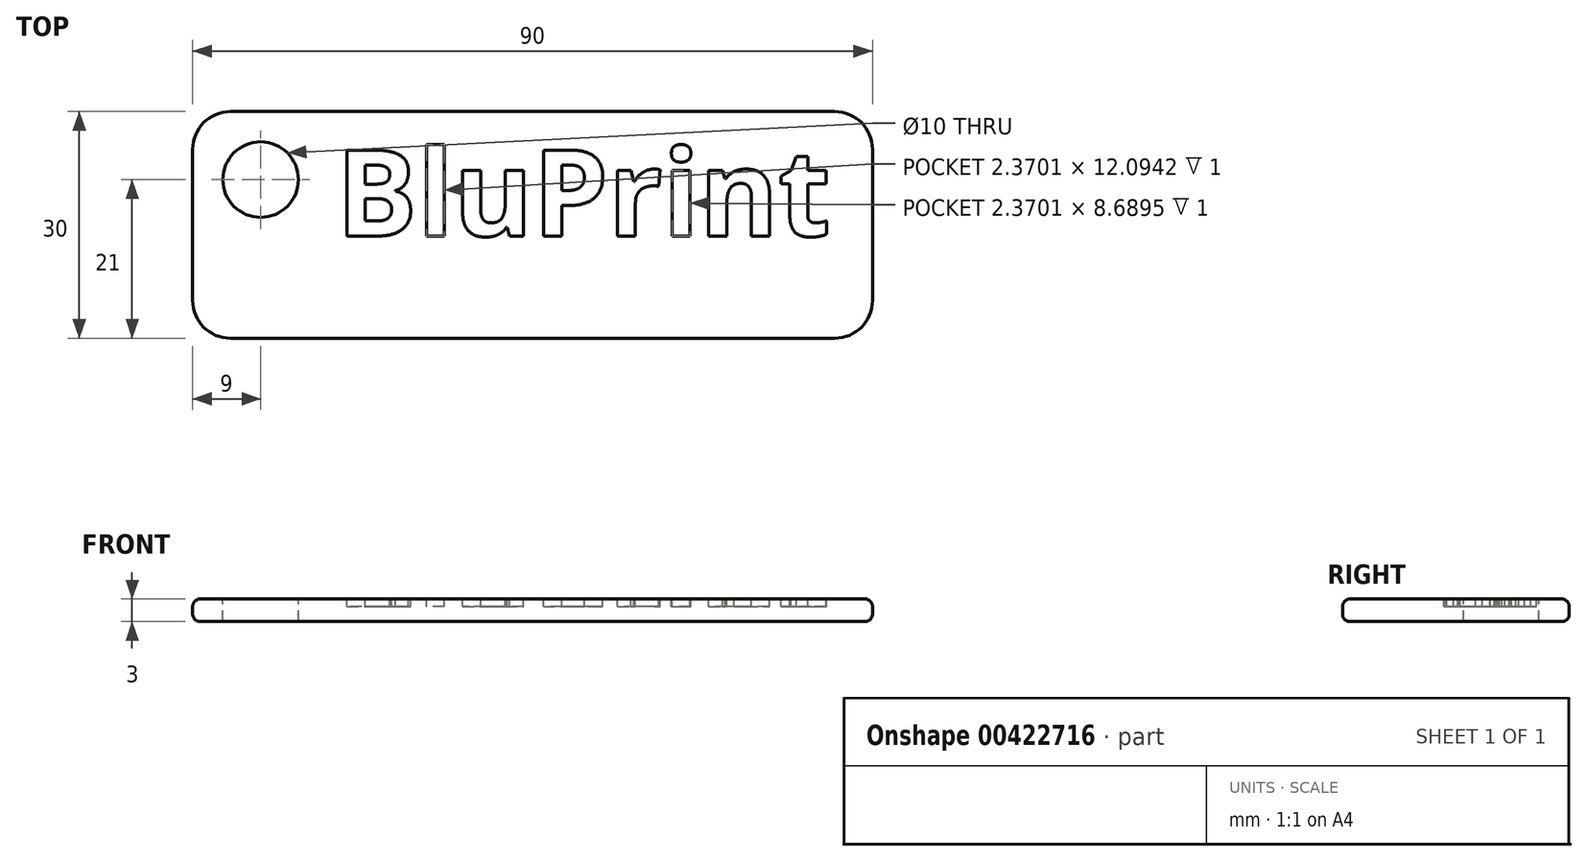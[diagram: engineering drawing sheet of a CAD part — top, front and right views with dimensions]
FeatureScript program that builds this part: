
annotation { "Feature Type Name" : "Feature", "Feature Type Description" : "" }
export const myFeature = defineFeature(function(context is Context, id is Id, definition is map)
    precondition{}
    {
        {
            var Q0;
            Q0=qCreatedBy(makeId("Top.planeOp"),FACE);
            var sketch = newSketch(context, id + "F0", { "sketchPlane" : qUnion([Q0])});
            skLineSegment(sketch, "E0.bottom", {"start": v(-45, 15) * mm, "end": v(45, 15) * mm});
            skLineSegment(sketch, "E0.top", {"start": v(-45, -15) * mm, "end": v(45, -15) * mm});
            skLineSegment(sketch, "E0.left", {"start": v(-45, 15) * mm, "end": v(-45, -15) * mm});
            skLineSegment(sketch, "E0.right", {"start": v(45, 15) * mm, "end": v(45, -15) * mm});
            skLineSegment(sketch, "E1", {"start": v(-45, 15) * mm, "end": v(45, -15) * mm, "construction": true});
            skSolve(sketch);
        }
        {
            var Q0;
            Q0=makeQuery(id+"F0.imprint","IMPRINT",FACE,{"disambiguationData":[TD([[makeQuery(id+"F0.imprint","IMPRINT",EDGE,{"derivedFrom":sQuery(id+"F0.wireOp",EDGE,"E0.bottom")}),-1.0]])]});
            extrude(context, id + "F1", {"entities" : qUnion([Q0]), "depth" : 3 * mm});
        }
        {
            var Q0;
            Q0=makeQuery(id+"F1.opExtrude","CAP_FACE",FACE,{"disambiguationData":[OSD([sQuery(id+"F0.wireOp",EDGE,"E0.bottom"),sQuery(id+"F0.wireOp",EDGE,"E0.top"),sQuery(id+"F0.wireOp",EDGE,"E0.left"),sQuery(id+"F0.wireOp",EDGE,"E0.right")])],"isStart":false});
            var Q1;
            Q1=makeQuery(id+"F1.opExtrude","CAP_FACE",FACE,{"disambiguationData":[OSD([sQuery(id+"F0.wireOp",EDGE,"E0.bottom"),sQuery(id+"F0.wireOp",EDGE,"E0.top"),sQuery(id+"F0.wireOp",EDGE,"E0.left"),sQuery(id+"F0.wireOp",EDGE,"E0.right")])],"isStart":true});
            fillet(context, id + "F2", {"entities" : qUnion([Q0, Q1]), "radius" : 1 * mm, "tangentPropagation" : true, "allowEdgeOverflow" : false});
        }
        {
            var Q0;
            Q0=makeQuery(id+"F1.opExtrude","SWEPT_EDGE",EDGE,{"disambiguationData":[OSD([sQuery(id+"F0.wireOp",EDGE,"E0.top"),sQuery(id+"F0.wireOp",EDGE,"E0.right")])]});
            var Q1;
            Q1=makeQuery(id+"F1.opExtrude","SWEPT_EDGE",EDGE,{"disambiguationData":[OSD([sQuery(id+"F0.wireOp",EDGE,"E0.bottom"),sQuery(id+"F0.wireOp",EDGE,"E0.right")])]});
            var Q2;
            Q2=makeQuery(id+"F1.opExtrude","SWEPT_EDGE",EDGE,{"disambiguationData":[OSD([sQuery(id+"F0.wireOp",EDGE,"E0.bottom"),sQuery(id+"F0.wireOp",EDGE,"E0.left")])]});
            var Q3;
            Q3=makeQuery(id+"F1.opExtrude","SWEPT_EDGE",EDGE,{"disambiguationData":[OSD([sQuery(id+"F0.wireOp",EDGE,"E0.top"),sQuery(id+"F0.wireOp",EDGE,"E0.left")])]});
            fillet(context, id + "F3", {"entities" : qUnion([Q0, Q1, Q2, Q3]), "radius" : 5 * mm, "tangentPropagation" : true, "allowEdgeOverflow" : false});
        }
        {
            var Q0;
            {var subQ0=sQuery(id+"F0.wireOp",EDGE,"E0.left");var subQ2=sQuery(id+"F0.wireOp",EDGE,"E0.bottom");var subQ4=sQuery(id+"F0.wireOp",EDGE,"E0.right");var subQ6=sQuery(id+"F0.wireOp",EDGE,"E0.top");Q0=makeQuery(id+"FmQCBBX3Ub0qneL_1.boolean.opBoolean","SPLIT",FACE,{"disambiguationData":[TD([makeQuery(id+"FmQCBBX3Ub0qneL_1.opExtrude","SWEPT_FACE",FACE,{"disambiguationData":[OSD([sQuery(id+"FOCoeRmDbjhRCuz_1.wireOp",EDGE,"4a1fb44a-e7be-4e23-9449-000d953c446c.sketch_text.stroke-0")])]})])],"derivedFrom":makeQuery(id+"F1.opExtrude","CAP_FACE",FACE,{"disambiguationData":[OSD([subQ2,subQ6,subQ0,subQ4])],"isStart":false})});}
            var sketch = newSketch(context, id + "F4", { "sketchPlane" : qUnion([Q0])});
            skCircle(sketch, "E2", {"center": v(-36, 6) * mm, "radius": 5 * mm});
            skSolve(sketch);
        }
        {
            var Q0;
            Q0=qSketchRegion(id+"F4",true);
            extrude(context, id + "F5", {"entities" : qUnion([Q0]), "operationType" : NewBodyOperationType.REMOVE, "oppositeDirection" : true, "depth" : 3 * mm});
        }
        {
            var Q0;
            Q0=makeQuery(id+"F1.opExtrude","CAP_FACE",FACE,{"disambiguationData":[OSD([sQuery(id+"F0.wireOp",EDGE,"E0.bottom"),sQuery(id+"F0.wireOp",EDGE,"E0.top"),sQuery(id+"F0.wireOp",EDGE,"E0.left"),sQuery(id+"F0.wireOp",EDGE,"E0.right")])],"isStart":false});
            var sketch = newSketch(context, id + "F6", { "sketchPlane" : qUnion([Q0])});
            skText(sketch, "E3", { "text": "BluPrint", "fontName": "OpenSans-Bold.ttf"});
            const initialGuessF6  = {"E3": [-0.026, -0.00146, 1, 0, 0.01146]};
            skSetInitialGuess(sketch, initialGuessF6);
            skSolve(sketch);
        }
        {
            var Q0;
            Q0=qSketchRegion(id+"F6",true);
            extrude(context, id + "F7", {"entities" : qUnion([Q0]), "operationType" : NewBodyOperationType.REMOVE, "oppositeDirection" : true, "depth" : 1 * mm});
        }
    });
